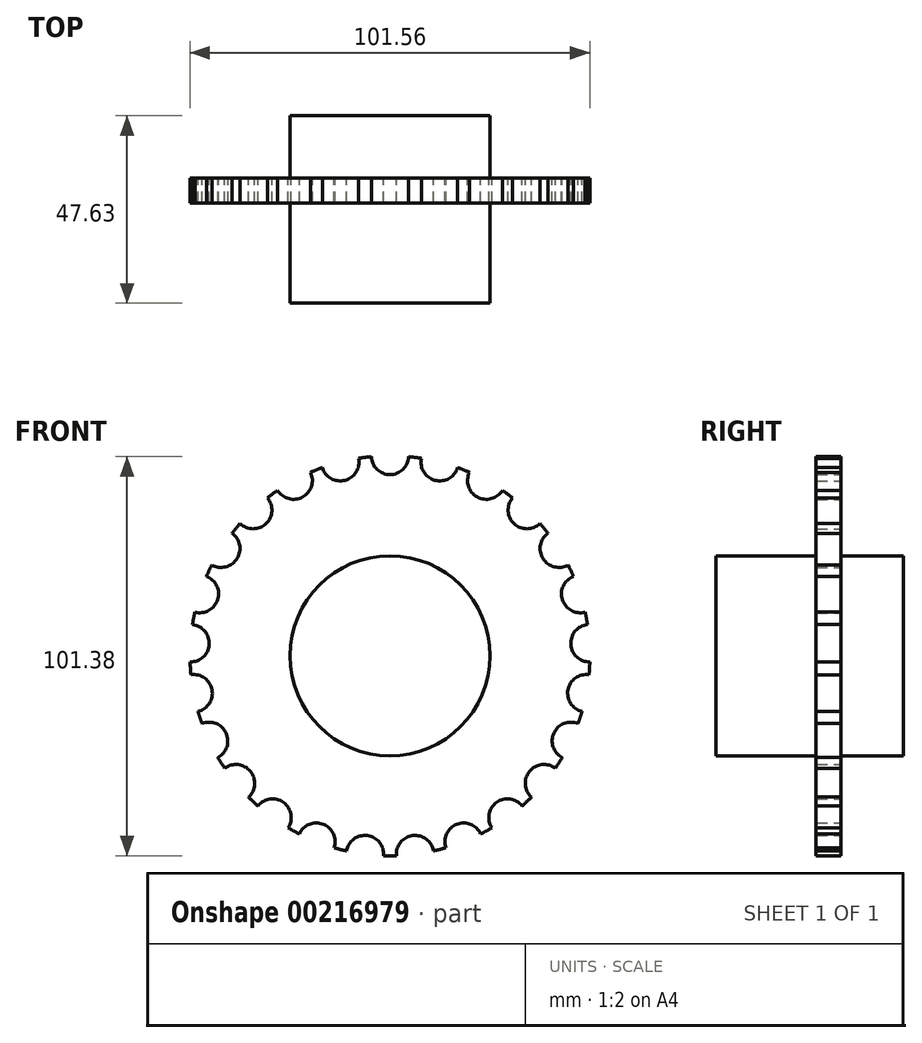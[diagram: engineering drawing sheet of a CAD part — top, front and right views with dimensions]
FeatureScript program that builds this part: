
annotation { "Feature Type Name" : "Feature", "Feature Type Description" : "" }
export const myFeature = defineFeature(function(context is Context, id is Id, definition is map)
    precondition{}
    {
        {
            var Q0;
            Q0=qCreatedBy(makeId("Front.planeOp"),FACE);
            var sketch = newSketch(context, id + "F0", { "sketchPlane" : qUnion([Q0])});
            skCircle(sketch, "E0", {"center": v(0, 0) * mm, "radius": 25.4 * mm});
            skCircle(sketch, "E1", {"center": v(0, 0) * mm, "radius": 50.8 * mm});
            skCircle(sketch, "E2", {"center": v(0, 50.8) * mm, "radius": 4.76 * mm});
            skCircle(sketch, "E3.1.0", {"center": v(-12.63, 49.2) * mm, "radius": 4.76 * mm});
            skCircle(sketch, "E3.2.0", {"center": v(-24.47, 44.52) * mm, "radius": 4.76 * mm});
            skCircle(sketch, "E3.3.0", {"center": v(-34.77, 37.03) * mm, "radius": 4.76 * mm});
            skCircle(sketch, "E3.4.0", {"center": v(-42.9, 27.22) * mm, "radius": 4.76 * mm});
            skCircle(sketch, "E3.5.0", {"center": v(-48.31, 15.7) * mm, "radius": 4.76 * mm});
            skCircle(sketch, "E3.6.0", {"center": v(-50.7, 3.19) * mm, "radius": 4.76 * mm});
            skCircle(sketch, "E3.7.0", {"center": v(-49.9, -9.52) * mm, "radius": 4.76 * mm});
            skCircle(sketch, "E3.8.0", {"center": v(-45.97, -21.63) * mm, "radius": 4.76 * mm});
            skCircle(sketch, "E3.9.0", {"center": v(-39.14, -32.38) * mm, "radius": 4.76 * mm});
            skCircle(sketch, "E3.10.0", {"center": v(-29.86, -41.1) * mm, "radius": 4.76 * mm});
            skCircle(sketch, "E3.11.0", {"center": v(-18.7, -47.23) * mm, "radius": 4.76 * mm});
            skCircle(sketch, "E3.12.0", {"center": v(-6.37, -50.4) * mm, "radius": 4.76 * mm});
            skCircle(sketch, "E3.13.0", {"center": v(6.37, -50.4) * mm, "radius": 4.76 * mm});
            skCircle(sketch, "E3.14.0", {"center": v(18.7, -47.23) * mm, "radius": 4.76 * mm});
            skCircle(sketch, "E3.15.0", {"center": v(29.86, -41.1) * mm, "radius": 4.76 * mm});
            skCircle(sketch, "E3.16.0", {"center": v(39.14, -32.38) * mm, "radius": 4.76 * mm});
            skCircle(sketch, "E3.17.0", {"center": v(45.97, -21.63) * mm, "radius": 4.76 * mm});
            skCircle(sketch, "E3.18.0", {"center": v(49.9, -9.52) * mm, "radius": 4.76 * mm});
            skCircle(sketch, "E3.19.0", {"center": v(50.7, 3.19) * mm, "radius": 4.76 * mm});
            skCircle(sketch, "E3.20.0", {"center": v(48.31, 15.7) * mm, "radius": 4.76 * mm});
            skCircle(sketch, "E3.21.0", {"center": v(42.9, 27.22) * mm, "radius": 4.76 * mm});
            skCircle(sketch, "E3.22.0", {"center": v(34.77, 37.03) * mm, "radius": 4.76 * mm});
            skCircle(sketch, "E3.23.0", {"center": v(24.47, 44.52) * mm, "radius": 4.76 * mm});
            skCircle(sketch, "E3.24.0", {"center": v(12.63, 49.2) * mm, "radius": 4.76 * mm});
            skSolve(sketch);
        }
        {
            var Q0;
            Q0=makeQuery(id+"F0.imprint","IMPRINT",FACE,{"disambiguationData":[TD([[makeQuery(id+"F0.imprint","IMPRINT",EDGE,{"derivedFrom":sQuery(id+"F0.wireOp",EDGE,"E0")}),-1.0]])]});
            extrude(context, id + "F1", {"entities" : qUnion([Q0]), "depth" : 6.35 * mm});
        }
        {
            var Q0;
            Q0=makeQuery(id+"F0.imprint","IMPRINT",FACE,{"disambiguationData":[TD([[makeQuery(id+"F0.imprint","IMPRINT",EDGE,{"derivedFrom":sQuery(id+"F0.wireOp",EDGE,"E0")}),1.0]])]});
            extrude(context, id + "F2", {"entities" : qUnion([Q0]), "operationType" : NewBodyOperationType.ADD, "depth" : 31.75 * mm, "hasSecondDirection" : true, "secondDirectionOppositeDirection" : true, "secondDirectionDepth" : 3.17 * mm});
        }
        {
            var Q0;
            Q0=makeQuery(id+"F2.opExtrude","CAP_FACE",FACE,{"disambiguationData":[OSD([sQuery(id+"F0.wireOp",EDGE,"E0")])],"isStart":true});
            extrude(context, id + "F3", {"entities" : qUnion([Q0]), "operationType" : NewBodyOperationType.ADD, "depth" : 12.7 * mm});
        }
    });
